# Revit family: LAMP_MUN DARK 180 SURFACE
name_source: partatom
category: Modelos genéricos
revit_build: Autodesk Revit 2015 (Build: 20140606_1530(x64)
units: mm (PartAtom-declared; Revit-internal decimal feet)

## types (4) — shared parameters
CRI = 80
Diameter = 180 mm  [stored 0.590551 ft]
Efficacy = 21 lm/W
Elevación por defecto = 1219 mm
Fabricante = LAMP
Gear = Electronic
Height = 47 mm  [stored 0.154199 ft]
IEE = A++
Initial intensity = 45 lm
Installation instructions = http://www.lamp.es
Insulation class = I
LED Lifetime = 50000 L70 B50
Lamp = OSRAM LED
Last update = 06/11/2020
Luminaire type = Indoor - Wall mounted
MacAdam = <3
Manufacturer URL = http://www.lamp.es
Manufacturer country = Spain
Manufacturer name = LAMP
Material difusor = LAMP_PC Difusor Opal MunDark
Photometric web file = Fotometria Mun Dark 180 : 3000K
Plum = 2 W
Power = 1 W
Power Supply = 100-127-240V 50-60Hz
Product URL = https://www.lamp.es
Product datasheet = http://www.lamp.es
Protection rating = IP20
Type = OSRAM
Weight = 0.62 kg

## per-type parameters (varying)
| type | Descripción | Finish | Initial color | Material base | Material cuerpo | Modelo | Product code |
| 45LM 4000 WHITE | MUN DARK Ø180 NW WH. | Texturised matte white | 4000 K | LAMP_Aluminio base MunDark WH | LAMP_Aluminio Mun Dark WH | MD1180SF0120840NW | MD1180SF0120840NW |
| 45LM 4000 GRAPHITE | MUN DARK Ø180 NW GRH. | Texturised matte graphite | 4000 K | LAMP_Aluminio base MunDark BL | LAMP_Aluminio Mun Dark BL | MD1180SF0120840NB | MD1180SF0120840NB |
| 45LM 3000 WHITE | MUN DARK Ø180 WW WH. | Texturised matte white | 3000 K | LAMP_Aluminio base MunDark WH | LAMP_Aluminio Mun Dark WH | MD1180SF0120830NW | MD1180SF0120830NW |
| 45LM 3000 GRAPHITE | MUN DARK Ø180 WW GRH. | Texturised matte graphite | 3000 K | LAMP_Aluminio base MunDark BL | LAMP_Aluminio Mun Dark BL | MD1180SF0120830NB | MD1180SF0120830NB |

note: [stored X ft] marks values corroborated as IEEE doubles in the binary element streams (Revit-internal decimal feet)
